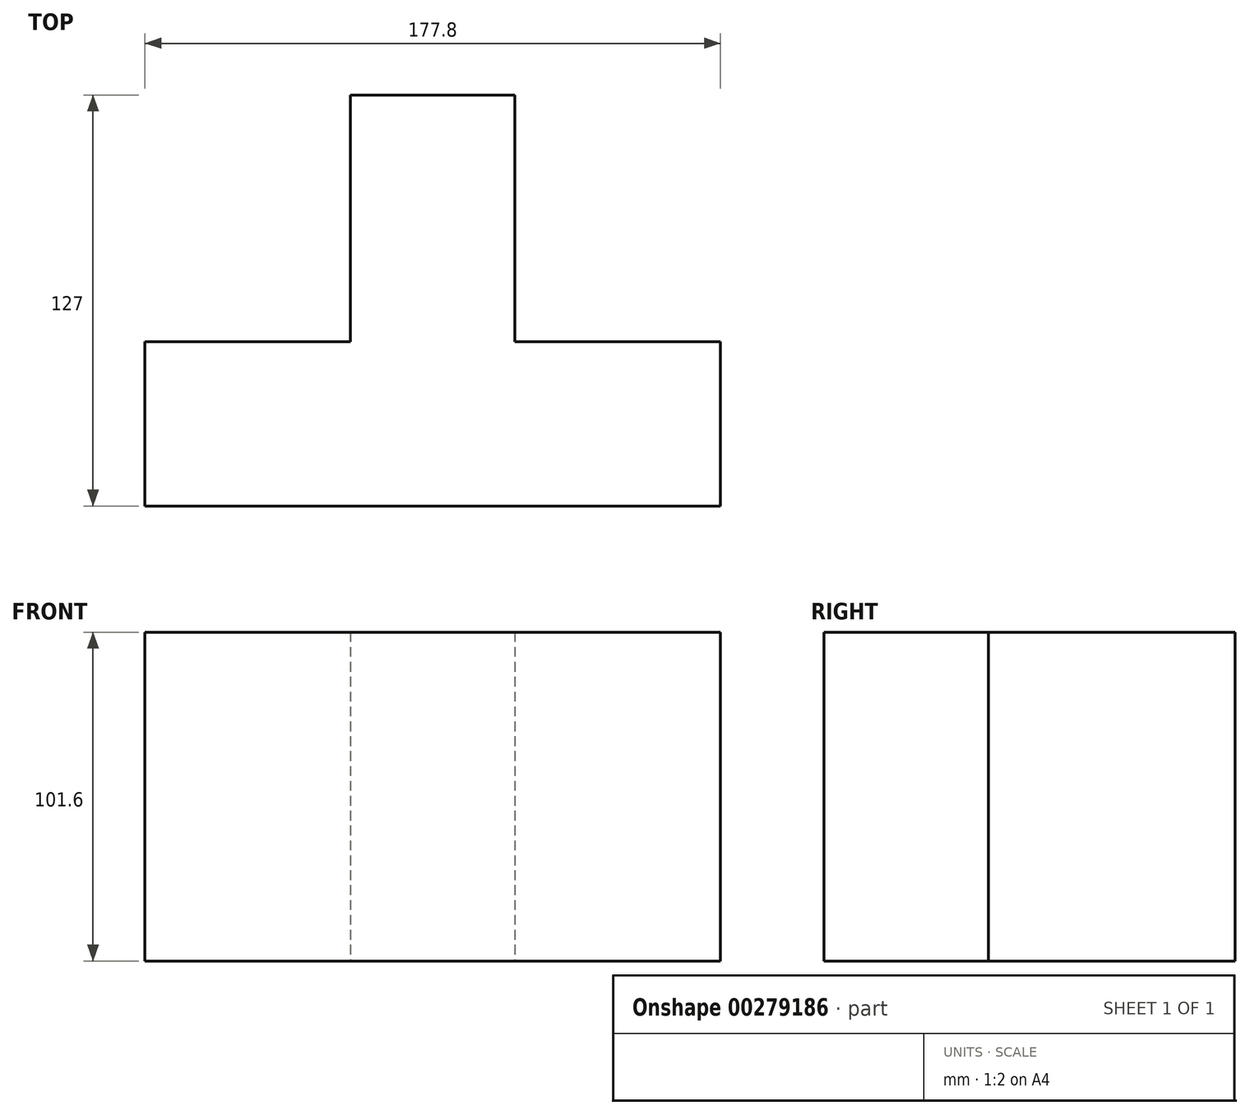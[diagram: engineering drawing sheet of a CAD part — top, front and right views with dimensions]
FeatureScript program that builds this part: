
annotation { "Feature Type Name" : "Feature", "Feature Type Description" : "" }
export const myFeature = defineFeature(function(context is Context, id is Id, definition is map)
    precondition{}
    {
        {
            var Q0;
            Q0=qCreatedBy(makeId("Top.planeOp"),FACE);
            var sketch = newSketch(context, id + "F0", { "sketchPlane" : qUnion([Q0])});
            skLineSegment(sketch, "E0", {"start": v(-39.11, 76.2) * mm, "end": v(11.69, 76.2) * mm});
            skLineSegment(sketch, "E1", {"start": v(11.69, 76.2) * mm, "end": v(11.69, 0) * mm});
            skLineSegment(sketch, "E2", {"start": v(11.69, 0) * mm, "end": v(75.19, 0) * mm});
            skLineSegment(sketch, "E3", {"start": v(75.19, 0) * mm, "end": v(75.19, -50.8) * mm});
            skLineSegment(sketch, "E4", {"start": v(75.19, -50.8) * mm, "end": v(-102.61, -50.8) * mm});
            skLineSegment(sketch, "E5", {"start": v(-102.61, -50.8) * mm, "end": v(-102.61, 0) * mm});
            skLineSegment(sketch, "E6", {"start": v(-102.61, 0) * mm, "end": v(-39.11, 0) * mm});
            skLineSegment(sketch, "E7", {"start": v(-39.11, 0) * mm, "end": v(-39.11, 76.2) * mm});
            skSolve(sketch);
        }
        {
            var Q0;
            Q0 = qSketchRegion(id + "F0", true);
            extrude(context, id + "F1", {"entities" : qUnion([Q0]), "depth" : 101.6 * mm});
        }
    });
